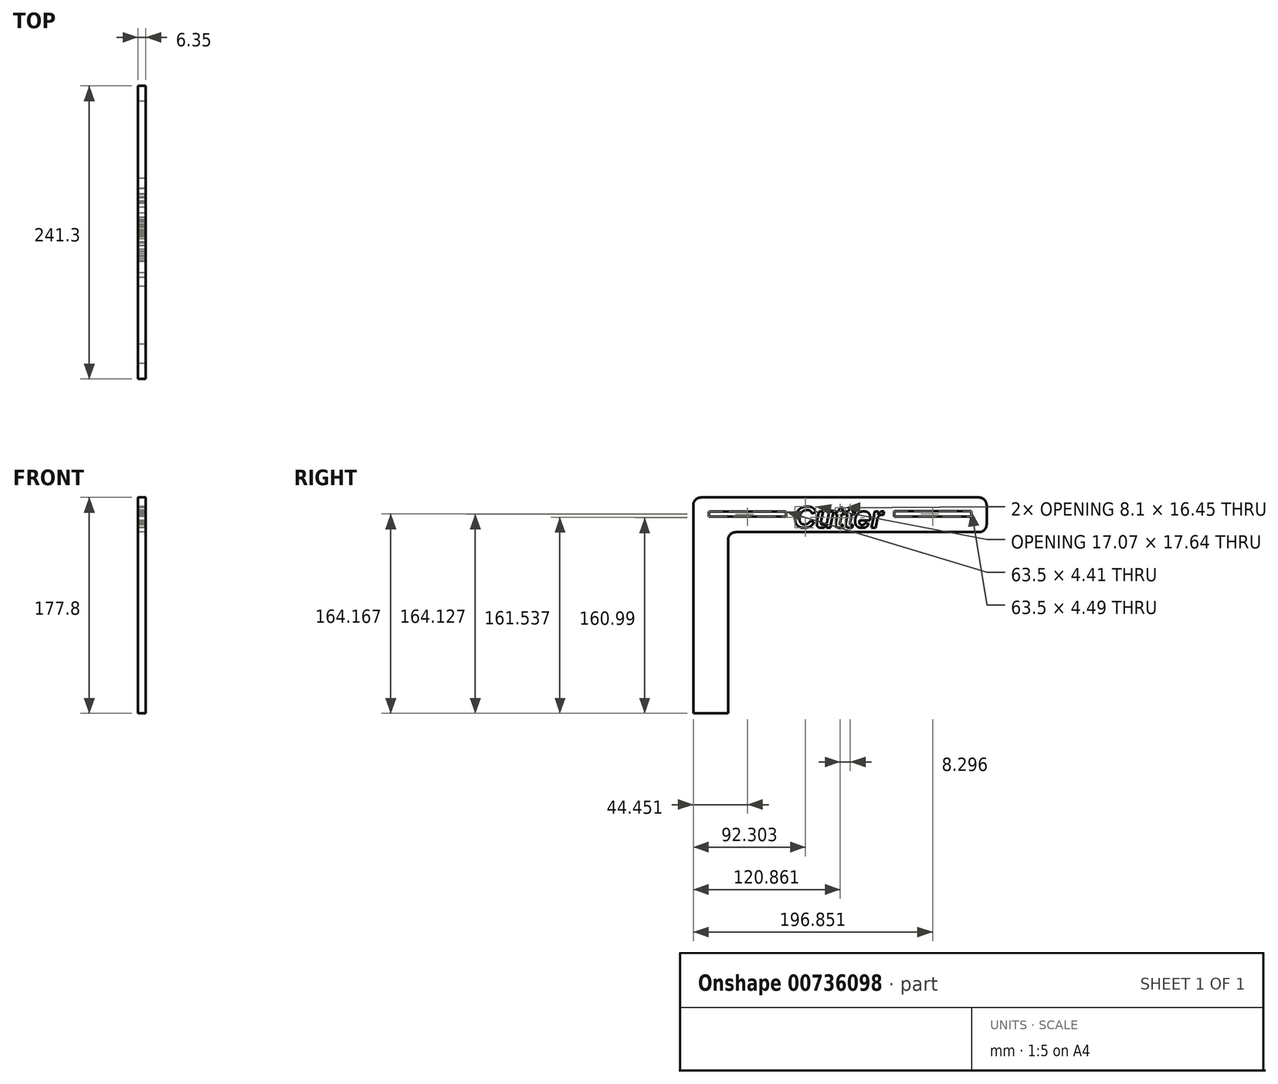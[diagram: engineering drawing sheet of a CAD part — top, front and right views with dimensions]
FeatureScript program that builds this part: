
annotation { "Feature Type Name" : "Feature", "Feature Type Description" : "" }
export const myFeature = defineFeature(function(context is Context, id is Id, definition is map)
    precondition{}
    {
        {
            var Q0;
            Q0=qCreatedBy(makeId("Right.planeOp"),FACE);
            var sketch = newSketch(context, id + "F0", { "sketchPlane" : qUnion([Q0])});
            skLineSegment(sketch, "E0.bottom", {"start": v(-136.49, 50.76) * mm, "end": v(-107.91, 50.76) * mm});
            skLineSegment(sketch, "E0.top", {"start": v(-136.49, -98.46) * mm, "end": v(-107.91, -98.46) * mm});
            skLineSegment(sketch, "E0.left", {"start": v(-136.49, 50.76) * mm, "end": v(-136.49, -98.46) * mm});
            skLineSegment(sketch, "E0.right", {"start": v(-107.91, 50.76) * mm, "end": v(-107.91, -98.46) * mm});
            skLineSegment(sketch, "E1.bottom", {"start": v(-136.49, 79.34) * mm, "end": v(104.81, 79.34) * mm});
            skLineSegment(sketch, "E1.top", {"start": v(-136.49, 50.76) * mm, "end": v(104.81, 50.76) * mm});
            skLineSegment(sketch, "E1.left", {"start": v(-136.49, 79.34) * mm, "end": v(-136.49, 50.76) * mm});
            skLineSegment(sketch, "E1.right", {"start": v(104.81, 79.34) * mm, "end": v(104.81, 50.76) * mm});
            skLineSegment(sketch, "E2.bottom", {"start": v(104.81, 50.76) * mm, "end": v(76.24, 50.76) * mm});
            skLineSegment(sketch, "E2.top", {"start": v(104.81, -98.46) * mm, "end": v(76.24, -98.46) * mm});
            skLineSegment(sketch, "E2.left", {"start": v(104.81, 50.76) * mm, "end": v(104.81, -98.46) * mm});
            skLineSegment(sketch, "E2.right", {"start": v(76.24, 50.76) * mm, "end": v(76.24, -98.46) * mm});
            skText(sketch, "E3", { "text": "Cutter", "fontName": "Arimo-BoldItalic.ttf"});
            skLineSegment(sketch, "E4.bottom", {"start": v(-123.79, 67.87) * mm, "end": v(-60.29, 67.87) * mm});
            skLineSegment(sketch, "E4.top", {"start": v(-123.79, 63.46) * mm, "end": v(-60.29, 63.46) * mm});
            skLineSegment(sketch, "E4.left", {"start": v(-123.79, 67.87) * mm, "end": v(-123.79, 63.46) * mm});
            skLineSegment(sketch, "E4.right", {"start": v(-60.29, 67.87) * mm, "end": v(-60.29, 63.46) * mm});
            skPoint(sketch, "E5.oppositeSnap0", {"position": v(-53.94, 63.46) * mm});
            skLineSegment(sketch, "E5.bottom", {"start": v(28.61, 67.95) * mm, "end": v(92.11, 67.95) * mm});
            skLineSegment(sketch, "E5.top", {"start": v(28.61, 63.46) * mm, "end": v(92.11, 63.46) * mm});
            skLineSegment(sketch, "E5.left", {"start": v(28.61, 67.95) * mm, "end": v(28.61, 63.46) * mm});
            skLineSegment(sketch, "E5.right", {"start": v(92.11, 67.95) * mm, "end": v(92.11, 63.46) * mm});
            const initialGuessF0  = {"E3": [-0.05394, 0.0545, 1, 0, 0.01794]};
            skSetInitialGuess(sketch, initialGuessF0);
            skSolve(sketch);
        }
        {
            var Q0;
            Q0=makeQuery(id+"F0.imprint","IMPRINT",FACE,{"disambiguationData":[TD([[makeQuery(id+"F0.imprint","IMPRINT",EDGE,{"derivedFrom":sQuery(id+"F0.wireOp",EDGE,"E1.bottom")}),-1.0]])]});
            var Q1;
            Q1=makeQuery(id+"F0.imprint","IMPRINT",FACE,{"disambiguationData":[TD([[makeQuery(id+"F0.imprint","IMPRINT",EDGE,{"derivedFrom":sQuery(id+"F0.wireOp",EDGE,"E0.top")}),1.0]])]});
            var Q2;
            Q2=makeQuery(id+"F0.imprint","IMPRINT",FACE,{"disambiguationData":[TD([[makeQuery(id+"F0.imprint","IMPRINT",EDGE,{"derivedFrom":sQuery(id+"F0.wireOp",EDGE,"E2.bottom")}),1.0]])]});
            extrude(context, id + "F1", {"entities" : qUnion([Q0, Q1, Q2]), "depth" : 6.35 * mm, "offsetDistance" : 25.4 * mm});
        }
        {
            var Q0;
            Q0=makeQuery(id+"F1.opExtrude","SWEPT_EDGE",EDGE,{"disambiguationData":[OSD([sQuery(id+"F0.wireOp",EDGE,"E1.bottom"),sQuery(id+"F0.wireOp",EDGE,"E1.left")])]});
            var Q1;
            Q1=makeQuery(id+"F1.opExtrude","SWEPT_EDGE",EDGE,{"disambiguationData":[OSD([sQuery(id+"F0.wireOp",EDGE,"E1.bottom"),sQuery(id+"F0.wireOp",EDGE,"E1.right")])]});
            var Q2;
            Q2=makeQuery(id+"F1.opExtrude","SWEPT_EDGE",EDGE,{"disambiguationData":[OSD([sQuery(id+"F0.wireOp",EDGE,"E0.right"),sQuery(id+"F0.wireOp",EDGE,"E1.top")])]});
            var Q3;
            Q3=makeQuery(id+"F1.opExtrude","SWEPT_EDGE",EDGE,{"disambiguationData":[OSD([sQuery(id+"F0.wireOp",EDGE,"E1.top"),sQuery(id+"F0.wireOp",EDGE,"E2.bottom"),sQuery(id+"F0.wireOp",EDGE,"E2.right")])]});
            fillet(context, id + "F2", {"entities" : qUnion([Q0, Q1, Q2, Q3]), "radius" : 6.35 * mm, "tangentPropagation" : true, "allowEdgeOverflow" : false});
        }
    });
